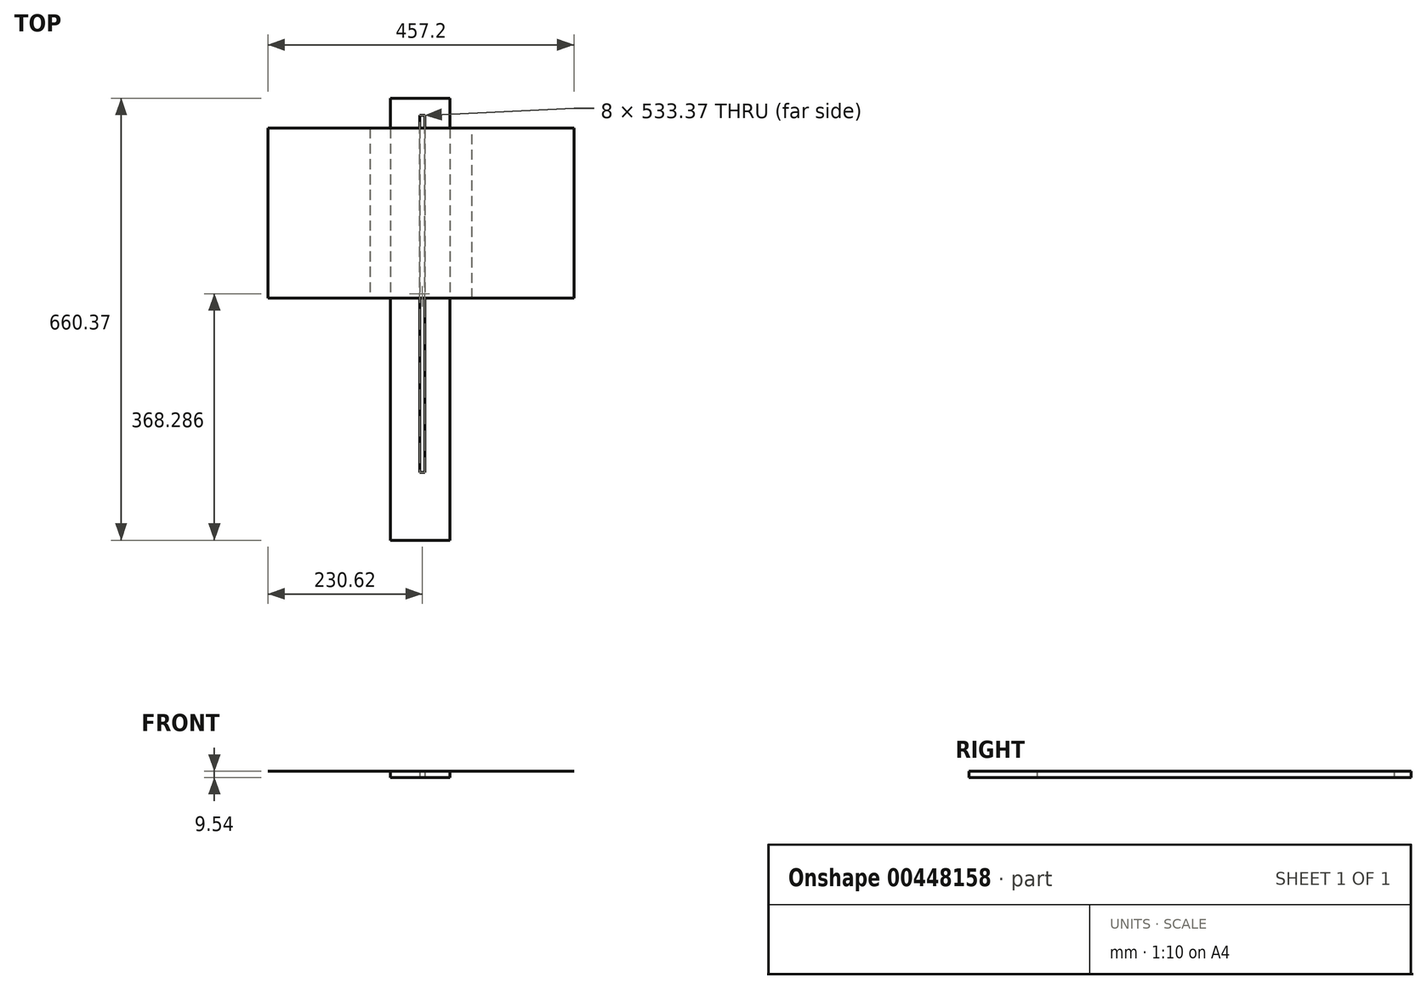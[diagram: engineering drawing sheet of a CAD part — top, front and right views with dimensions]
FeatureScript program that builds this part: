
annotation { "Feature Type Name" : "Feature", "Feature Type Description" : "" }
export const myFeature = defineFeature(function(context is Context, id is Id, definition is map)
    precondition{}
    {
        {
            var Q0;
            Q0=qCreatedBy(makeId("Top.planeOp"),FACE);
            var sketch = newSketch(context, id + "F0", { "sketchPlane" : qUnion([Q0])});
            skLineSegment(sketch, "E0.bottom", {"start": v(-230.62, -156.73) * mm, "end": v(226.58, -156.73) * mm});
            skLineSegment(sketch, "E0.top", {"start": v(-230.62, 97.27) * mm, "end": v(226.58, 97.27) * mm});
            skLineSegment(sketch, "E0.left", {"start": v(-230.62, -156.73) * mm, "end": v(-230.62, 97.27) * mm});
            skLineSegment(sketch, "E0.right", {"start": v(226.58, -156.73) * mm, "end": v(226.58, 97.27) * mm});
            skSolve(sketch);
        }
        {
            var Q0;
            Q0=makeQuery(id+"F0.imprint","IMPRINT",FACE,{"disambiguationData":[TD([[makeQuery(id+"F0.imprint","IMPRINT",EDGE,{"derivedFrom":sQuery(id+"F0.wireOp",EDGE,"E0.bottom")}),1.0]])]});
            extrude(context, id + "F1", {"entities" : qUnion([Q0]), "depth" : 3 / 203.2 * mm});
        }
        {
            var Q0;
            Q0=makeQuery(id+"F1.opExtrude","CAP_FACE",FACE,{"disambiguationData":[OSD([sQuery(id+"F0.wireOp",EDGE,"E0.bottom"),sQuery(id+"F0.wireOp",EDGE,"E0.top"),sQuery(id+"F0.wireOp",EDGE,"E0.left"),sQuery(id+"F0.wireOp",EDGE,"E0.right")])],"isStart":true});
            var sketch = newSketch(context, id + "F2", { "sketchPlane" : qUnion([Q0])});
            skLineSegment(sketch, "E1.bottom", {"start": v(-230.62, -97.27) * mm, "end": v(-78.22, -97.27) * mm});
            skLineSegment(sketch, "E1.top", {"start": v(-230.62, 156.73) * mm, "end": v(-78.22, 156.73) * mm});
            skLineSegment(sketch, "E1.left", {"start": v(-230.62, -97.27) * mm, "end": v(-230.62, 156.73) * mm});
            skLineSegment(sketch, "E1.right", {"start": v(-78.22, -97.27) * mm, "end": v(-78.22, 156.73) * mm});
            skLineSegment(sketch, "E2.bottom", {"start": v(226.58, 156.73) * mm, "end": v(74.18, 156.73) * mm});
            skLineSegment(sketch, "E2.top", {"start": v(226.58, -97.27) * mm, "end": v(74.18, -97.27) * mm});
            skLineSegment(sketch, "E2.left", {"start": v(226.58, 156.73) * mm, "end": v(226.58, -97.27) * mm});
            skLineSegment(sketch, "E2.right", {"start": v(74.18, 156.73) * mm, "end": v(74.18, -97.27) * mm});
            skSolve(sketch);
        }
        {
            var Q0;
            Q0=makeQuery(id+"F2.imprint","IMPRINT",FACE,{"disambiguationData":[TD([[makeQuery(id+"F2.imprint","IMPRINT",EDGE,{"derivedFrom":sQuery(id+"F2.wireOp",EDGE,"E1.bottom")}),1.0]])]});
            var Q1;
            Q1=makeQuery(id+"F2.imprint","IMPRINT",FACE,{"disambiguationData":[TD([[makeQuery(id+"F2.imprint","IMPRINT",EDGE,{"derivedFrom":sQuery(id+"F2.wireOp",EDGE,"E2.bottom")}),-1.0]])]});
            extrude(context, id + "F3", {"entities" : qUnion([Q0, Q1]), "operationType" : NewBodyOperationType.ADD, "depth" : 3 / 203.2 * mm});
        }
        {
            var Q0;
            Q0=makeQuery(id+"F1.opExtrude","CAP_FACE",FACE,{"disambiguationData":[OSD([sQuery(id+"F0.wireOp",EDGE,"E0.bottom"),sQuery(id+"F0.wireOp",EDGE,"E0.top"),sQuery(id+"F0.wireOp",EDGE,"E0.left"),sQuery(id+"F0.wireOp",EDGE,"E0.right")])],"isStart":true});
            var sketch = newSketch(context, id + "F4", { "sketchPlane" : qUnion([Q0])});
            skLineSegment(sketch, "E3", {"start": v(0, -142.15) * mm, "end": v(0, 518.22) * mm, "construction": true});
            skLineSegment(sketch, "E4.bottom", {"start": v(41.26, -142.15) * mm, "end": v(-47.64, -142.15) * mm});
            skLineSegment(sketch, "E4.top", {"start": v(41.26, 518.22) * mm, "end": v(-47.64, 518.22) * mm});
            skLineSegment(sketch, "E4.left", {"start": v(41.26, -142.15) * mm, "end": v(41.26, 518.22) * mm});
            skLineSegment(sketch, "E4.right", {"start": v(-47.64, -142.15) * mm, "end": v(-47.64, 518.22) * mm});
            skSolve(sketch);
        }
        {
            var Q0;
            Q0 = qSketchRegion(id + "F4", true);
            extrude(context, id + "F5", {"entities" : qUnion([Q0]), "depth" : 9.52 * mm});
        }
        {
            var Q0;
            Q0=makeQuery(id+"F5.opExtrude","CAP_FACE",FACE,{"disambiguationData":[OSD([sQuery(id+"F4.wireOp",EDGE,"E4.bottom"),sQuery(id+"F4.wireOp",EDGE,"E4.top"),sQuery(id+"F4.wireOp",EDGE,"E4.left"),sQuery(id+"F4.wireOp",EDGE,"E4.right")])],"isStart":false});
            var sketch = newSketch(context, id + "F6", { "sketchPlane" : qUnion([Q0])});
            skLineSegment(sketch, "E5", {"start": v(0, -116.75) * mm, "end": v(0, 416.62) * mm, "construction": true});
            skLineSegment(sketch, "E6.bottom", {"start": v(4, 416.62) * mm, "end": v(-4, 416.62) * mm});
            skLineSegment(sketch, "E6.top", {"start": v(4, -116.75) * mm, "end": v(-4, -116.75) * mm});
            skLineSegment(sketch, "E6.left", {"start": v(4, 416.62) * mm, "end": v(4, -116.75) * mm});
            skLineSegment(sketch, "E6.right", {"start": v(-4, 416.62) * mm, "end": v(-4, -116.75) * mm});
            skSolve(sketch);
        }
        {
            var Q0;
            Q0 = qSketchRegion(id + "F6", true);
            extrude(context, id + "F7", {"entities" : qUnion([Q0]), "operationType" : NewBodyOperationType.REMOVE, "endBound" : BoundingType.UP_TO_NEXT, "oppositeDirection" : true, "depth" : 25.4 * mm});
        }
    });
